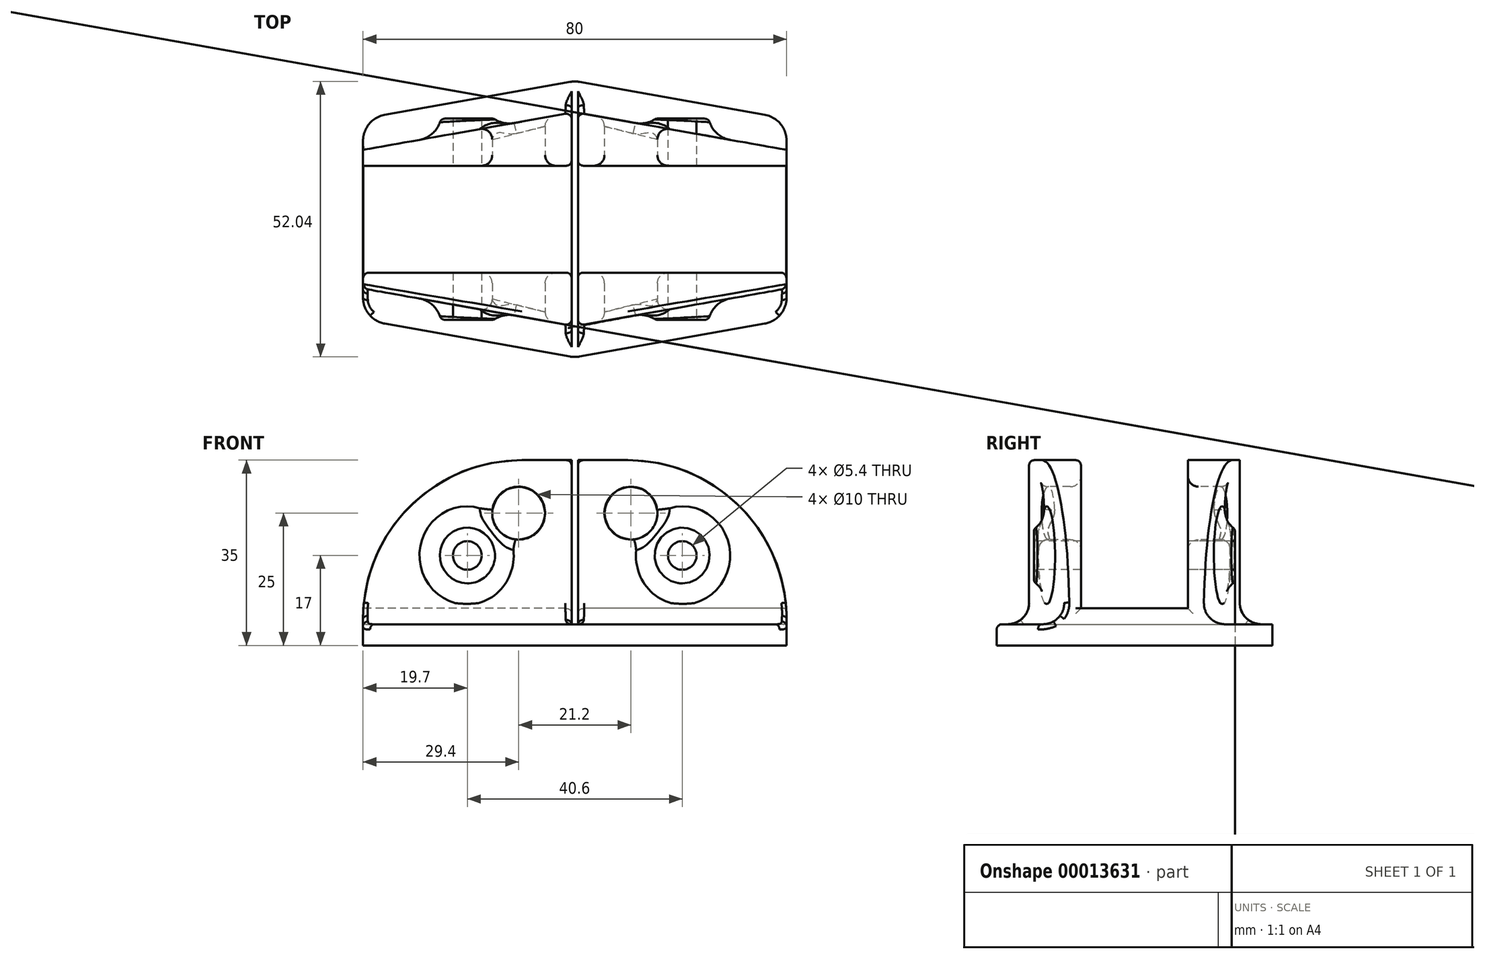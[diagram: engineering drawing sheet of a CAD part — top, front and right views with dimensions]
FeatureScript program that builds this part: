
annotation { "Feature Type Name" : "Feature", "Feature Type Description" : "" }
export const myFeature = defineFeature(function(context is Context, id is Id, definition is map)
    precondition{}
    {
        {
            var Q0;
            Q0=qCreatedBy(makeId("Top.planeOp"),FACE);
            var sketch = newSketch(context, id + "F0", { "sketchPlane" : qUnion([Q0])});
            skLineSegment(sketch, "E0.rect.bottom", {"start": v(40, 10.1) * mm, "end": v(-40, 10.1) * mm});
            skLineSegment(sketch, "E0.rect.top", {"start": v(40, -10.1) * mm, "end": v(-40, -10.1) * mm});
            skLineSegment(sketch, "E0.rect.left", {"start": v(40, 10.1) * mm, "end": v(40, -10.1) * mm});
            skLineSegment(sketch, "E0.rect.right", {"start": v(-40, 10.1) * mm, "end": v(-40, -10.1) * mm});
            skPoint(sketch, "E0.rect.middle", {"position": v(0, 0) * mm});
            skLineSegment(sketch, "E1", {"start": v(-40, 20.1) * mm, "end": v(40, 20.1) * mm, "construction": true});
            skLineSegment(sketch, "E2", {"start": v(40, -20.1) * mm, "end": v(-40, -20.1) * mm, "construction": true});
            skLineSegment(sketch, "E3", {"start": v(40, 10.1) * mm, "end": v(40, 20.1) * mm});
            skLineSegment(sketch, "E4", {"start": v(40, -10.1) * mm, "end": v(40, -20.1) * mm});
            skLineSegment(sketch, "E5.rect.bottom", {"start": v(0.6, 20.1) * mm, "end": v(-0.6, 20.1) * mm});
            skLineSegment(sketch, "E5.rect.top", {"start": v(0.6, -20.1) * mm, "end": v(-0.6, -20.1) * mm});
            skLineSegment(sketch, "E5.rect.left", {"start": v(0.6, 20.1) * mm, "end": v(0.6, 10.1) * mm});
            skLineSegment(sketch, "E5.rect.right", {"start": v(-0.6, 20.1) * mm, "end": v(-0.6, 10.1) * mm});
            skLineSegment(sketch, "E6", {"start": v(-40, -10.1) * mm, "end": v(-40, -20.1) * mm});
            skLineSegment(sketch, "E7", {"start": v(-40, 10.1) * mm, "end": v(-40, 20.1) * mm});
            skLineSegment(sketch, "E8.trimOffspring", {"start": v(0.6, -10.1) * mm, "end": v(0.6, -20.1) * mm});
            skLineSegment(sketch, "E9.trimOffspring", {"start": v(-0.6, -10.1) * mm, "end": v(-0.6, -20.1) * mm});
            skLineSegment(sketch, "E10", {"start": v(-40, 26.1) * mm, "end": v(40, 26.1) * mm, "construction": true});
            skLineSegment(sketch, "E11", {"start": v(40, -26.1) * mm, "end": v(-40, -26.1) * mm, "construction": true});
            skLineSegment(sketch, "E12", {"start": v(40, -20.1) * mm, "end": v(40, -26.1) * mm});
            skLineSegment(sketch, "E13", {"start": v(-40, -26.1) * mm, "end": v(-40, -20.1) * mm});
            skLineSegment(sketch, "E14", {"start": v(-40, 20.1) * mm, "end": v(-40, 26.1) * mm});
            skLineSegment(sketch, "E15", {"start": v(40, 26.1) * mm, "end": v(40, 20.1) * mm});
            skLineSegment(sketch, "E16", {"start": v(0.6, 10.1) * mm, "end": v(0.6, -10.1) * mm});
            skLineSegment(sketch, "E17", {"start": v(-0.6, -10.1) * mm, "end": v(-0.6, 10.1) * mm});
            skLineSegment(sketch, "E18", {"start": v(0.6, 20.1) * mm, "end": v(40, 13.1) * mm});
            skLineSegment(sketch, "E19", {"start": v(-0.6, 20.1) * mm, "end": v(-40, 13.1) * mm});
            skLineSegment(sketch, "E20", {"start": v(40, -13.1) * mm, "end": v(0.6, -20.1) * mm});
            skLineSegment(sketch, "E21", {"start": v(-0.6, -20.1) * mm, "end": v(-40, -13.1) * mm});
            skLineSegment(sketch, "E22", {"start": v(0, 26.1) * mm, "end": v(40, 19) * mm});
            skLineSegment(sketch, "E23", {"start": v(0, 26.1) * mm, "end": v(-40, 19) * mm});
            skLineSegment(sketch, "E24", {"start": v(0, -26.1) * mm, "end": v(40, -19) * mm});
            skLineSegment(sketch, "E25", {"start": v(0, -26.1) * mm, "end": v(-40, -19) * mm});
            skSolve(sketch);
        }
        {
            var Q0;
            Q0=makeQuery(id+"F0.imprint","IMPRINT",FACE,{"disambiguationData":[TD([[makeQuery(id+"F0.imprint","IMPRINT",EDGE,{"derivedFrom":sQuery(id+"F0.wireOp",EDGE,"E5.rect.bottom")}),-1.0]])]});
            var Q1;
            {var subQ4=sQuery(id+"F0.wireOp",EDGE,"E5.rect.right");Q1=makeQuery(id+"F0.imprint","IMPRINT",FACE,{"disambiguationData":[TD([[makeQuery(id+"F0.imprint","IMPRINT",EDGE,{"derivedFrom":subQ4}),-1.0]])]});}
            var Q2;
            Q2=makeQuery(id+"F0.imprint","IMPRINT",FACE,{"disambiguationData":[TD([[makeQuery(id+"F0.imprint","IMPRINT",EDGE,{"derivedFrom":sQuery(id+"F0.wireOp",EDGE,"E5.rect.bottom")}),1.0]])]});
            var Q3;
            {var subQ1=sQuery(id+"F0.wireOp",EDGE,"E5.rect.left");Q3=makeQuery(id+"F0.imprint","IMPRINT",FACE,{"disambiguationData":[TD([[makeQuery(id+"F0.imprint","IMPRINT",EDGE,{"derivedFrom":subQ1}),1.0]])]});}
            var Q4;
            {var subQ1=sQuery(id+"F0.wireOp",EDGE,"E0.rect.left");Q4=makeQuery(id+"F0.imprint","IMPRINT",FACE,{"disambiguationData":[TD([[makeQuery(id+"F0.imprint","IMPRINT",EDGE,{"derivedFrom":subQ1}),-1.0]])]});}
            var Q5;
            Q5=makeQuery(id+"F0.imprint","IMPRINT",FACE,{"disambiguationData":[TD([[makeQuery(id+"F0.imprint","IMPRINT",EDGE,{"derivedFrom":sQuery(id+"F0.wireOp",EDGE,"E5.rect.top")}),-1.0]])]});
            var Q6;
            {var subQ1=sQuery(id+"F0.wireOp",EDGE,"E9.trimOffspring");Q6=makeQuery(id+"F0.imprint","IMPRINT",FACE,{"disambiguationData":[TD([[makeQuery(id+"F0.imprint","IMPRINT",EDGE,{"derivedFrom":subQ1}),-1.0]])]});}
            var Q7;
            {var subQ1=sQuery(id+"F0.wireOp",EDGE,"E8.trimOffspring");Q7=makeQuery(id+"F0.imprint","IMPRINT",FACE,{"disambiguationData":[TD([[makeQuery(id+"F0.imprint","IMPRINT",EDGE,{"derivedFrom":subQ1}),1.0]])]});}
            var Q8;
            Q8=makeQuery(id+"F0.imprint","IMPRINT",FACE,{"disambiguationData":[TD([[makeQuery(id+"F0.imprint","IMPRINT",EDGE,{"derivedFrom":sQuery(id+"F0.wireOp",EDGE,"E5.rect.top")}),1.0]])]});
            var Q9;
            {var subQ1=sQuery(id+"F0.wireOp",EDGE,"E16");Q9=makeQuery(id+"F0.imprint","IMPRINT",FACE,{"disambiguationData":[TD([[makeQuery(id+"F0.imprint","IMPRINT",EDGE,{"derivedFrom":subQ1}),-1.0]])]});}
            var Q10;
            {var subQ1=sQuery(id+"F0.wireOp",EDGE,"E0.rect.right");Q10=makeQuery(id+"F0.imprint","IMPRINT",FACE,{"disambiguationData":[TD([[makeQuery(id+"F0.imprint","IMPRINT",EDGE,{"derivedFrom":subQ1}),1.0]])]});}
            extrude(context, id + "F1", {"entities" : qUnion([Q0, Q1, Q2, Q3, Q4, Q5, Q6, Q7, Q8, Q9, Q10]), "depth" : 4 * mm});
        }
        {
            var Q0;
            {var subQ1=sQuery(id+"F0.wireOp",EDGE,"E9.trimOffspring");Q0=makeQuery(id+"F0.imprint","IMPRINT",FACE,{"disambiguationData":[TD([[makeQuery(id+"F0.imprint","IMPRINT",EDGE,{"derivedFrom":subQ1}),-1.0]])]});}
            var Q1;
            {var subQ1=sQuery(id+"F0.wireOp",EDGE,"E8.trimOffspring");Q1=makeQuery(id+"F0.imprint","IMPRINT",FACE,{"disambiguationData":[TD([[makeQuery(id+"F0.imprint","IMPRINT",EDGE,{"derivedFrom":subQ1}),1.0]])]});}
            var Q2;
            {var subQ1=sQuery(id+"F0.wireOp",EDGE,"E5.rect.left");Q2=makeQuery(id+"F0.imprint","IMPRINT",FACE,{"disambiguationData":[TD([[makeQuery(id+"F0.imprint","IMPRINT",EDGE,{"derivedFrom":subQ1}),1.0]])]});}
            var Q3;
            {var subQ4=sQuery(id+"F0.wireOp",EDGE,"E5.rect.right");Q3=makeQuery(id+"F0.imprint","IMPRINT",FACE,{"disambiguationData":[TD([[makeQuery(id+"F0.imprint","IMPRINT",EDGE,{"derivedFrom":subQ4}),-1.0]])]});}
            extrude(context, id + "F2", {"entities" : qUnion([Q0, Q1, Q2, Q3]), "operationType" : NewBodyOperationType.ADD, "depth" : 35 * mm});
        }
        {
            var Q0;
            {var subQ1=sQuery(id+"F0.wireOp",EDGE,"E0.rect.right");Q0=makeQuery(id+"F0.imprint","IMPRINT",FACE,{"disambiguationData":[TD([[makeQuery(id+"F0.imprint","IMPRINT",EDGE,{"derivedFrom":subQ1}),1.0]])]});}
            var Q1;
            {var subQ1=sQuery(id+"F0.wireOp",EDGE,"E0.rect.left");Q1=makeQuery(id+"F0.imprint","IMPRINT",FACE,{"disambiguationData":[TD([[makeQuery(id+"F0.imprint","IMPRINT",EDGE,{"derivedFrom":subQ1}),-1.0]])]});}
            extrude(context, id + "F3", {"entities" : qUnion([Q0, Q1]), "operationType" : NewBodyOperationType.ADD, "depth" : 7 * mm});
        }
        {
            var Q0;
            Q0=qCreatedBy(makeId("Front.planeOp"),FACE);
            var sketch = newSketch(context, id + "F4", { "sketchPlane" : qUnion([Q0])});
            skLineSegment(sketch, "E26.0", {"start": v(-0.6, 7) * mm, "end": v(-40, 7) * mm});
            skLineSegment(sketch, "E27.0", {"start": v(40, 7) * mm, "end": v(0.6, 7) * mm});
            skLineSegment(sketch, "E28", {"start": v(-20.3, 7) * mm, "end": v(-20.3, 17) * mm, "construction": true});
            skLineSegment(sketch, "E29", {"start": v(20.3, 7) * mm, "end": v(20.3, 17) * mm, "construction": true});
            skCircle(sketch, "E30", {"center": v(-20.3, 17) * mm, "radius": 2.7 * mm});
            skCircle(sketch, "E31", {"center": v(20.3, 17) * mm, "radius": 2.7 * mm});
            skCircle(sketch, "E32", {"center": v(-20.3, 17) * mm, "radius": 5 * mm});
            skCircle(sketch, "E33", {"center": v(20.3, 17) * mm, "radius": 5 * mm});
            skCircle(sketch, "E34", {"center": v(-10.6, 25) * mm, "radius": 5 * mm});
            skCircle(sketch, "E35", {"center": v(10.6, 25) * mm, "radius": 5 * mm});
            skLineSegment(sketch, "E36.0", {"start": v(-0.6, 35) * mm, "end": v(-0.6, 7) * mm});
            skLineSegment(sketch, "E37.0", {"start": v(0.6, 35) * mm, "end": v(0.6, 7) * mm});
            skLineSegment(sketch, "E38", {"start": v(-10.6, 25) * mm, "end": v(-0.6, 25) * mm, "construction": true});
            skLineSegment(sketch, "E39", {"start": v(10.6, 25) * mm, "end": v(0.6, 25) * mm, "construction": true});
            skSolve(sketch);
        }
        {
            var Q0;
            Q0=makeQuery(id+"F4.imprint","IMPRINT",FACE,{"disambiguationData":[TD([[makeQuery(id+"F4.imprint","IMPRINT",EDGE,{"derivedFrom":sQuery(id+"F4.wireOp",EDGE,"E30")}),1.0]])]});
            var Q1;
            Q1=makeQuery(id+"F4.imprint","IMPRINT",FACE,{"disambiguationData":[TD([[makeQuery(id+"F4.imprint","IMPRINT",EDGE,{"derivedFrom":sQuery(id+"F4.wireOp",EDGE,"E31")}),1.0]])]});
            extrude(context, id + "F5", {"entities" : qUnion([Q0, Q1]), "operationType" : NewBodyOperationType.REMOVE, "oppositeDirection" : true, "depth" : 50 * mm, "symmetric" : true});
        }
        {
            var Q0;
            Q0=makeQuery(id+"F4.imprint","IMPRINT",FACE,{"disambiguationData":[TD([[makeQuery(id+"F4.imprint","IMPRINT",EDGE,{"derivedFrom":sQuery(id+"F4.wireOp",EDGE,"E30")}),-1.0]])]});
            var Q1;
            Q1=makeQuery(id+"F4.imprint","IMPRINT",FACE,{"disambiguationData":[TD([[makeQuery(id+"F4.imprint","IMPRINT",EDGE,{"derivedFrom":sQuery(id+"F4.wireOp",EDGE,"E31")}),-1.0]])]});
            extrude(context, id + "F6", {"entities" : qUnion([Q0, Q1]), "operationType" : NewBodyOperationType.ADD, "depth" : 38 * mm, "symmetric" : true});
        }
        {
            var Q0;
            Q0=makeQuery(id+"F4.imprint","IMPRINT",FACE,{"disambiguationData":[TD([[makeQuery(id+"F4.imprint","IMPRINT",EDGE,{"derivedFrom":sQuery(id+"F4.wireOp",EDGE,"E30")}),-1.0]])]});
            var Q1;
            Q1=makeQuery(id+"F4.imprint","IMPRINT",FACE,{"disambiguationData":[TD([[makeQuery(id+"F4.imprint","IMPRINT",EDGE,{"derivedFrom":sQuery(id+"F4.wireOp",EDGE,"E31")}),-1.0]])]});
            extrude(context, id + "F7", {"entities" : qUnion([Q0, Q1]), "operationType" : NewBodyOperationType.REMOVE, "oppositeDirection" : true, "depth" : 20.2 * mm, "symmetric" : true});
        }
        {
            var Q0;
            Q0=makeQuery(id+"F4.imprint","IMPRINT",FACE,{"disambiguationData":[TD([[makeQuery(id+"F4.imprint","IMPRINT",EDGE,{"derivedFrom":sQuery(id+"F4.wireOp",EDGE,"E34")}),1.0]])]});
            var Q1;
            Q1=makeQuery(id+"F4.imprint","IMPRINT",FACE,{"disambiguationData":[TD([[makeQuery(id+"F4.imprint","IMPRINT",EDGE,{"derivedFrom":sQuery(id+"F4.wireOp",EDGE,"E35")}),1.0]])]});
            extrude(context, id + "F8", {"entities" : qUnion([Q0, Q1]), "operationType" : NewBodyOperationType.REMOVE, "oppositeDirection" : true, "depth" : 50 * mm, "symmetric" : true});
        }
        {
            var Q0;
            Q0=makeQuery(id+"F2.opExtrude","CAP_EDGE",EDGE,{"disambiguationData":[OSD([sQuery(id+"F0.wireOp",EDGE,"E4")])],"isStart":false});
            var Q1;
            Q1=makeQuery(id+"F2.opExtrude","CAP_EDGE",EDGE,{"disambiguationData":[OSD([sQuery(id+"F0.wireOp",EDGE,"E6")])],"isStart":false});
            var Q2;
            Q2=makeQuery(id+"F2.opExtrude","CAP_EDGE",EDGE,{"disambiguationData":[OSD([sQuery(id+"F0.wireOp",EDGE,"E7")])],"isStart":false});
            var Q3;
            Q3=makeQuery(id+"F2.opExtrude","CAP_EDGE",EDGE,{"disambiguationData":[OSD([sQuery(id+"F0.wireOp",EDGE,"E3")])],"isStart":false});
            fillet(context, id + "F9", {"entities" : qUnion([Q0, Q1, Q2, Q3]), "radius" : 30 * mm, "tangentPropagation" : true, "allowEdgeOverflow" : false});
        }
        {
            var Q0;
            Q0=makeQuery(id+"F1.opExtrude","SWEPT_EDGE",EDGE,{"disambiguationData":[OSD([sQuery(id+"F0.wireOp",EDGE,"E7"),sQuery(id+"F0.wireOp",EDGE,"E23")])]});
            var Q1;
            Q1=makeQuery(id+"F1.opExtrude","SWEPT_EDGE",EDGE,{"disambiguationData":[OSD([sQuery(id+"F0.wireOp",EDGE,"E6"),sQuery(id+"F0.wireOp",EDGE,"E25")])]});
            var Q2;
            Q2=makeQuery(id+"F1.opExtrude","SWEPT_EDGE",EDGE,{"disambiguationData":[OSD([sQuery(id+"F0.wireOp",EDGE,"E22"),sQuery(id+"F0.wireOp",EDGE,"E23")])]});
            var Q3;
            Q3=makeQuery(id+"F1.opExtrude","SWEPT_EDGE",EDGE,{"disambiguationData":[OSD([sQuery(id+"F0.wireOp",EDGE,"E3"),sQuery(id+"F0.wireOp",EDGE,"E22")])]});
            var Q4;
            Q4=makeQuery(id+"F1.opExtrude","SWEPT_EDGE",EDGE,{"disambiguationData":[OSD([sQuery(id+"F0.wireOp",EDGE,"E4"),sQuery(id+"F0.wireOp",EDGE,"E24")])]});
            var Q5;
            Q5=makeQuery(id+"F1.opExtrude","SWEPT_EDGE",EDGE,{"disambiguationData":[OSD([sQuery(id+"F0.wireOp",EDGE,"E24"),sQuery(id+"F0.wireOp",EDGE,"E25")])]});
            fillet(context, id + "F10", {"entities" : qUnion([Q0, Q1, Q2, Q3, Q4, Q5]), "radius" : 5 * mm, "tangentPropagation" : true, "allowEdgeOverflow" : false});
        }
        {
            var Q0;
            Q0=makeQuery(id+"F2.boolean.opBoolean","INTERSECT",EDGE,{"derivedFrom":[makeQuery(id+"F1.opExtrude","CAP_FACE",FACE,{"disambiguationData":[OSD([sQuery(id+"F0.wireOp",EDGE,"E0.rect.left"),sQuery(id+"F0.wireOp",EDGE,"E0.rect.right"),sQuery(id+"F0.wireOp",EDGE,"E3"),sQuery(id+"F0.wireOp",EDGE,"E4"),sQuery(id+"F0.wireOp",EDGE,"E6"),sQuery(id+"F0.wireOp",EDGE,"E7"),sQuery(id+"F0.wireOp",EDGE,"E22"),sQuery(id+"F0.wireOp",EDGE,"E23"),sQuery(id+"F0.wireOp",EDGE,"E24"),sQuery(id+"F0.wireOp",EDGE,"E25")])],"isStart":false}),makeQuery(id+"F2.opExtrude","SWEPT_FACE",FACE,{"disambiguationData":[OSD([sQuery(id+"F0.wireOp",EDGE,"E21")])]})]});
            var Q1;
            Q1=makeQuery(id+"F2.boolean.opBoolean","INTERSECT",EDGE,{"derivedFrom":[makeQuery(id+"F1.opExtrude","CAP_FACE",FACE,{"disambiguationData":[OSD([sQuery(id+"F0.wireOp",EDGE,"E0.rect.left"),sQuery(id+"F0.wireOp",EDGE,"E0.rect.right"),sQuery(id+"F0.wireOp",EDGE,"E3"),sQuery(id+"F0.wireOp",EDGE,"E4"),sQuery(id+"F0.wireOp",EDGE,"E6"),sQuery(id+"F0.wireOp",EDGE,"E7"),sQuery(id+"F0.wireOp",EDGE,"E22"),sQuery(id+"F0.wireOp",EDGE,"E23"),sQuery(id+"F0.wireOp",EDGE,"E24"),sQuery(id+"F0.wireOp",EDGE,"E25")])],"isStart":false}),makeQuery(id+"F2.opExtrude","SWEPT_FACE",FACE,{"disambiguationData":[OSD([sQuery(id+"F0.wireOp",EDGE,"E20")])]})]});
            var Q2;
            Q2=makeQuery(id+"F2.boolean.opBoolean","INTERSECT",EDGE,{"derivedFrom":[makeQuery(id+"F1.opExtrude","CAP_FACE",FACE,{"disambiguationData":[OSD([sQuery(id+"F0.wireOp",EDGE,"E0.rect.left"),sQuery(id+"F0.wireOp",EDGE,"E0.rect.right"),sQuery(id+"F0.wireOp",EDGE,"E3"),sQuery(id+"F0.wireOp",EDGE,"E4"),sQuery(id+"F0.wireOp",EDGE,"E6"),sQuery(id+"F0.wireOp",EDGE,"E7"),sQuery(id+"F0.wireOp",EDGE,"E22"),sQuery(id+"F0.wireOp",EDGE,"E23"),sQuery(id+"F0.wireOp",EDGE,"E24"),sQuery(id+"F0.wireOp",EDGE,"E25")])],"isStart":false}),makeQuery(id+"F2.opExtrude","SWEPT_FACE",FACE,{"disambiguationData":[OSD([sQuery(id+"F0.wireOp",EDGE,"E19")])]})]});
            var Q3;
            Q3=makeQuery(id+"F2.boolean.opBoolean","INTERSECT",EDGE,{"derivedFrom":[makeQuery(id+"F1.opExtrude","CAP_FACE",FACE,{"disambiguationData":[OSD([sQuery(id+"F0.wireOp",EDGE,"E0.rect.left"),sQuery(id+"F0.wireOp",EDGE,"E0.rect.right"),sQuery(id+"F0.wireOp",EDGE,"E3"),sQuery(id+"F0.wireOp",EDGE,"E4"),sQuery(id+"F0.wireOp",EDGE,"E6"),sQuery(id+"F0.wireOp",EDGE,"E7"),sQuery(id+"F0.wireOp",EDGE,"E22"),sQuery(id+"F0.wireOp",EDGE,"E23"),sQuery(id+"F0.wireOp",EDGE,"E24"),sQuery(id+"F0.wireOp",EDGE,"E25")])],"isStart":false}),makeQuery(id+"F2.opExtrude","SWEPT_FACE",FACE,{"disambiguationData":[OSD([sQuery(id+"F0.wireOp",EDGE,"E18")])]})]});
            fillet(context, id + "F11", {"entities" : qUnion([Q0, Q1, Q2, Q3]), "radius" : 4 * mm, "tangentPropagation" : true, "allowEdgeOverflow" : false});
        }
        {
            var Q0;
            Q0=makeQuery(id+"F11.opFillet","BLEND_EDGE",EDGE,{"blendedFrom":[makeQuery(id+"F2.boolean.opBoolean","INTERSECT",EDGE,{"derivedFrom":[makeQuery(id+"F1.opExtrude","CAP_FACE",FACE,{"disambiguationData":[OSD([sQuery(id+"F0.wireOp",EDGE,"E0.rect.left"),sQuery(id+"F0.wireOp",EDGE,"E0.rect.right"),sQuery(id+"F0.wireOp",EDGE,"E3"),sQuery(id+"F0.wireOp",EDGE,"E4"),sQuery(id+"F0.wireOp",EDGE,"E6"),sQuery(id+"F0.wireOp",EDGE,"E7"),sQuery(id+"F0.wireOp",EDGE,"E22"),sQuery(id+"F0.wireOp",EDGE,"E23"),sQuery(id+"F0.wireOp",EDGE,"E24"),sQuery(id+"F0.wireOp",EDGE,"E25")])],"isStart":false}),makeQuery(id+"F2.opExtrude","SWEPT_FACE",FACE,{"disambiguationData":[OSD([sQuery(id+"F0.wireOp",EDGE,"E18")])]})]}),makeQuery(id+"F3.boolean.opBoolean","MERGE",FACE,{"derivedFrom":[makeQuery(id+"F2.opExtrude","SWEPT_FACE",FACE,{"disambiguationData":[OSD([sQuery(id+"F0.wireOp",EDGE,"E5.rect.left")])]}),makeQuery(id+"F2.opExtrude","SWEPT_FACE",FACE,{"disambiguationData":[OSD([sQuery(id+"F0.wireOp",EDGE,"E8.trimOffspring")])]}),makeQuery(id+"F3.opExtrude","SWEPT_FACE",FACE,{"disambiguationData":[OSD([sQuery(id+"F0.wireOp",EDGE,"E16")])]})]})],"blendedInto":[makeQuery(id+"F3.boolean.opBoolean","MERGE",FACE,{"derivedFrom":[makeQuery(id+"F2.opExtrude","SWEPT_FACE",FACE,{"disambiguationData":[OSD([sQuery(id+"F0.wireOp",EDGE,"E5.rect.left")])]}),makeQuery(id+"F2.opExtrude","SWEPT_FACE",FACE,{"disambiguationData":[OSD([sQuery(id+"F0.wireOp",EDGE,"E8.trimOffspring")])]}),makeQuery(id+"F3.opExtrude","SWEPT_FACE",FACE,{"disambiguationData":[OSD([sQuery(id+"F0.wireOp",EDGE,"E16")])]})]})]});
            var Q1;
            Q1=makeQuery(id+"F11.opFillet","BLEND_EDGE",EDGE,{"blendedFrom":[makeQuery(id+"F2.boolean.opBoolean","INTERSECT",EDGE,{"derivedFrom":[makeQuery(id+"F1.opExtrude","CAP_FACE",FACE,{"disambiguationData":[OSD([sQuery(id+"F0.wireOp",EDGE,"E0.rect.left"),sQuery(id+"F0.wireOp",EDGE,"E0.rect.right"),sQuery(id+"F0.wireOp",EDGE,"E3"),sQuery(id+"F0.wireOp",EDGE,"E4"),sQuery(id+"F0.wireOp",EDGE,"E6"),sQuery(id+"F0.wireOp",EDGE,"E7"),sQuery(id+"F0.wireOp",EDGE,"E22"),sQuery(id+"F0.wireOp",EDGE,"E23"),sQuery(id+"F0.wireOp",EDGE,"E24"),sQuery(id+"F0.wireOp",EDGE,"E25")])],"isStart":false}),makeQuery(id+"F2.opExtrude","SWEPT_FACE",FACE,{"disambiguationData":[OSD([sQuery(id+"F0.wireOp",EDGE,"E19")])]})]}),makeQuery(id+"F3.boolean.opBoolean","MERGE",FACE,{"derivedFrom":[makeQuery(id+"F2.opExtrude","SWEPT_FACE",FACE,{"disambiguationData":[OSD([sQuery(id+"F0.wireOp",EDGE,"E5.rect.right")])]}),makeQuery(id+"F2.opExtrude","SWEPT_FACE",FACE,{"disambiguationData":[OSD([sQuery(id+"F0.wireOp",EDGE,"E9.trimOffspring")])]}),makeQuery(id+"F3.opExtrude","SWEPT_FACE",FACE,{"disambiguationData":[OSD([sQuery(id+"F0.wireOp",EDGE,"E17")])]})]})],"blendedInto":[makeQuery(id+"F3.boolean.opBoolean","MERGE",FACE,{"derivedFrom":[makeQuery(id+"F2.opExtrude","SWEPT_FACE",FACE,{"disambiguationData":[OSD([sQuery(id+"F0.wireOp",EDGE,"E5.rect.right")])]}),makeQuery(id+"F2.opExtrude","SWEPT_FACE",FACE,{"disambiguationData":[OSD([sQuery(id+"F0.wireOp",EDGE,"E9.trimOffspring")])]}),makeQuery(id+"F3.opExtrude","SWEPT_FACE",FACE,{"disambiguationData":[OSD([sQuery(id+"F0.wireOp",EDGE,"E17")])]})]})]});
            var Q2;
            Q2=makeQuery(id+"F2.opExtrude","SWEPT_EDGE",EDGE,{"disambiguationData":[OSD([sQuery(id+"F0.wireOp",EDGE,"E0.rect.bottom"),sQuery(id+"F0.wireOp",EDGE,"E5.rect.right"),sQuery(id+"F0.wireOp",EDGE,"E17")])]});
            var Q3;
            Q3=makeQuery(id+"F2.opExtrude","SWEPT_EDGE",EDGE,{"disambiguationData":[OSD([sQuery(id+"F0.wireOp",EDGE,"E0.rect.bottom"),sQuery(id+"F0.wireOp",EDGE,"E5.rect.left"),sQuery(id+"F0.wireOp",EDGE,"E16")])]});
            var Q4;
            Q4=makeQuery(id+"F2.opExtrude","SWEPT_EDGE",EDGE,{"disambiguationData":[OSD([sQuery(id+"F0.wireOp",EDGE,"E5.rect.top"),sQuery(id+"F0.wireOp",EDGE,"E8.trimOffspring"),sQuery(id+"F0.wireOp",EDGE,"E20")])]});
            var Q5;
            Q5=makeQuery(id+"F2.opExtrude","SWEPT_EDGE",EDGE,{"disambiguationData":[OSD([sQuery(id+"F0.wireOp",EDGE,"E5.rect.top"),sQuery(id+"F0.wireOp",EDGE,"E9.trimOffspring"),sQuery(id+"F0.wireOp",EDGE,"E21")])]});
            var Q6;
            Q6=makeQuery(id+"F2.opExtrude","SWEPT_EDGE",EDGE,{"disambiguationData":[OSD([sQuery(id+"F0.wireOp",EDGE,"E0.rect.top"),sQuery(id+"F0.wireOp",EDGE,"E9.trimOffspring"),sQuery(id+"F0.wireOp",EDGE,"E17")])]});
            var Q7;
            Q7=makeQuery(id+"F2.opExtrude","SWEPT_EDGE",EDGE,{"disambiguationData":[OSD([sQuery(id+"F0.wireOp",EDGE,"E0.rect.top"),sQuery(id+"F0.wireOp",EDGE,"E8.trimOffspring"),sQuery(id+"F0.wireOp",EDGE,"E16")])]});
            var Q8;
            Q8=makeQuery(id+"F3.opExtrude","CAP_EDGE",EDGE,{"disambiguationData":[OSD([sQuery(id+"F0.wireOp",EDGE,"E17")])],"isStart":false});
            var Q9;
            Q9=makeQuery(id+"F3.opExtrude","CAP_EDGE",EDGE,{"disambiguationData":[OSD([sQuery(id+"F0.wireOp",EDGE,"E16")])],"isStart":false});
            var Q10;
            {var subQ0=sQuery(id+"F0.wireOp",EDGE,"E0.rect.top");Q10=makeQuery(id+"F3.opExtrude","CAP_EDGE",EDGE,{"disambiguationData":[OSD([subQ0]),TDD([makeQuery(id+"F0.imprint","IMPRINT",EDGE,{"disambiguationData":[TD([[makeQuery(id+"F0.imprint","INTERSECT",VERTEX,{"derivedFrom":[subQ0,sQuery(id+"F0.wireOp",EDGE,"E0.rect.left"),sQuery(id+"F0.wireOp",EDGE,"E4")]}),-1.0]])],"derivedFrom":subQ0})])],"isStart":false});}
            var Q11;
            {var subQ0=sQuery(id+"F0.wireOp",EDGE,"E0.rect.bottom");Q11=makeQuery(id+"F3.opExtrude","CAP_EDGE",EDGE,{"disambiguationData":[OSD([subQ0]),TDD([makeQuery(id+"F0.imprint","IMPRINT",EDGE,{"disambiguationData":[TD([[makeQuery(id+"F0.imprint","INTERSECT",VERTEX,{"derivedFrom":[subQ0,sQuery(id+"F0.wireOp",EDGE,"E0.rect.left"),sQuery(id+"F0.wireOp",EDGE,"E3")]}),-1.0]])],"derivedFrom":subQ0})])],"isStart":false});}
            var Q12;
            {var subQ0=sQuery(id+"F0.wireOp",EDGE,"E0.rect.bottom");Q12=makeQuery(id+"F3.opExtrude","CAP_EDGE",EDGE,{"disambiguationData":[OSD([subQ0]),TDD([makeQuery(id+"F0.imprint","IMPRINT",EDGE,{"disambiguationData":[TD([[makeQuery(id+"F0.imprint","INTERSECT",VERTEX,{"derivedFrom":[subQ0,sQuery(id+"F0.wireOp",EDGE,"E0.rect.right"),sQuery(id+"F0.wireOp",EDGE,"E7")]}),1.0]])],"derivedFrom":subQ0})])],"isStart":false});}
            var Q13;
            {var subQ0=sQuery(id+"F0.wireOp",EDGE,"E0.rect.top");Q13=makeQuery(id+"F3.opExtrude","CAP_EDGE",EDGE,{"disambiguationData":[OSD([subQ0]),TDD([makeQuery(id+"F0.imprint","IMPRINT",EDGE,{"disambiguationData":[TD([[makeQuery(id+"F0.imprint","INTERSECT",VERTEX,{"derivedFrom":[subQ0,sQuery(id+"F0.wireOp",EDGE,"E0.rect.right"),sQuery(id+"F0.wireOp",EDGE,"E6")]}),1.0]])],"derivedFrom":subQ0})])],"isStart":false});}
            var Q14;
            Q14=makeQuery(id+"F3.opExtrude","CAP_EDGE",EDGE,{"disambiguationData":[OSD([sQuery(id+"F0.wireOp",EDGE,"E0.rect.right")])],"isStart":false});
            var Q15;
            Q15=makeQuery(id+"F3.opExtrude","CAP_EDGE",EDGE,{"disambiguationData":[OSD([sQuery(id+"F0.wireOp",EDGE,"E0.rect.left")])],"isStart":false});
            fillet(context, id + "F12", {"entities" : qUnion([Q0, Q1, Q2, Q3, Q4, Q5, Q6, Q7, Q8, Q9, Q10, Q11, Q12, Q13, Q14, Q15]), "radius" : 1 * mm, "tangentPropagation" : true, "allowEdgeOverflow" : false});
        }
        {
            var Q0;
            Q0=makeQuery(id+"F9.opFillet","BLEND_EDGE",EDGE,{"blendedFrom":[makeQuery(id+"F2.opExtrude","CAP_EDGE",EDGE,{"disambiguationData":[OSD([sQuery(id+"F0.wireOp",EDGE,"E4")])],"isStart":false}),makeQuery(id+"F2.opExtrude","SWEPT_FACE",FACE,{"disambiguationData":[OSD([sQuery(id+"F0.wireOp",EDGE,"E20")])]})],"blendedInto":[makeQuery(id+"F2.opExtrude","SWEPT_FACE",FACE,{"disambiguationData":[OSD([sQuery(id+"F0.wireOp",EDGE,"E20")])]})]});
            var Q1;
            {var subQ0=sQuery(id+"F0.wireOp",EDGE,"E3");var subQ1=sQuery(id+"F0.wireOp",EDGE,"E18");Q1=makeQuery(id+"F9.opFillet","BLEND_EDGE",EDGE,{"blendedFrom":[makeQuery(id+"F2.opExtrude","CAP_EDGE",EDGE,{"disambiguationData":[OSD([subQ0])],"isStart":false}),makeQuery(id+"F6.boolean.opBoolean","SPLIT",FACE,{"disambiguationData":[TD([makeQuery(id+"F2.opExtrude","SWEPT_FACE",FACE,{"disambiguationData":[OSD([subQ0])]})])],"derivedFrom":makeQuery(id+"F2.opExtrude","SWEPT_FACE",FACE,{"disambiguationData":[OSD([subQ1])]})})],"blendedInto":[makeQuery(id+"F6.boolean.opBoolean","SPLIT",FACE,{"disambiguationData":[TD([makeQuery(id+"F2.opExtrude","SWEPT_FACE",FACE,{"disambiguationData":[OSD([subQ0])]})])],"derivedFrom":makeQuery(id+"F2.opExtrude","SWEPT_FACE",FACE,{"disambiguationData":[OSD([subQ1])]})})]});}
            var Q2;
            Q2=makeQuery(id+"F9.opFillet","BLEND_EDGE",EDGE,{"blendedFrom":[makeQuery(id+"F2.opExtrude","CAP_EDGE",EDGE,{"disambiguationData":[OSD([sQuery(id+"F0.wireOp",EDGE,"E7")])],"isStart":false}),makeQuery(id+"F2.opExtrude","SWEPT_FACE",FACE,{"disambiguationData":[OSD([sQuery(id+"F0.wireOp",EDGE,"E19")])]})],"blendedInto":[makeQuery(id+"F2.opExtrude","SWEPT_FACE",FACE,{"disambiguationData":[OSD([sQuery(id+"F0.wireOp",EDGE,"E19")])]})]});
            var Q3;
            {var subQ0=sQuery(id+"F0.wireOp",EDGE,"E6");var subQ1=sQuery(id+"F0.wireOp",EDGE,"E21");Q3=makeQuery(id+"F9.opFillet","BLEND_EDGE",EDGE,{"blendedFrom":[makeQuery(id+"F2.opExtrude","CAP_EDGE",EDGE,{"disambiguationData":[OSD([subQ0])],"isStart":false}),makeQuery(id+"F6.boolean.opBoolean","SPLIT",FACE,{"disambiguationData":[TD([makeQuery(id+"F2.opExtrude","SWEPT_FACE",FACE,{"disambiguationData":[OSD([sQuery(id+"F0.wireOp",EDGE,"E5.rect.right")])]})])],"derivedFrom":makeQuery(id+"F2.opExtrude","SWEPT_FACE",FACE,{"disambiguationData":[OSD([subQ1])]})})],"blendedInto":[makeQuery(id+"F6.boolean.opBoolean","SPLIT",FACE,{"disambiguationData":[TD([makeQuery(id+"F2.opExtrude","SWEPT_FACE",FACE,{"disambiguationData":[OSD([sQuery(id+"F0.wireOp",EDGE,"E5.rect.right")])]})])],"derivedFrom":makeQuery(id+"F2.opExtrude","SWEPT_FACE",FACE,{"disambiguationData":[OSD([subQ1])]})})]});}
            fillet(context, id + "F13", {"entities" : qUnion([Q0, Q1, Q2, Q3]), "radius" : 1 * mm, "tangentPropagation" : true, "allowEdgeOverflow" : false});
        }
        {
            var Q0;
            Q0=makeQuery(id+"F6.boolean.opBoolean","INTERSECT",EDGE,{"derivedFrom":[makeQuery(id+"F2.opExtrude","SWEPT_FACE",FACE,{"disambiguationData":[OSD([sQuery(id+"F0.wireOp",EDGE,"E18")])]}),makeQuery(id+"F6.opExtrude","SWEPT_FACE",FACE,{"disambiguationData":[OSD([sQuery(id+"F4.wireOp",EDGE,"E33")])]})]});
            var Q1;
            Q1=makeQuery(id+"F6.boolean.opBoolean","INTERSECT",EDGE,{"derivedFrom":[makeQuery(id+"F2.opExtrude","SWEPT_FACE",FACE,{"disambiguationData":[OSD([sQuery(id+"F0.wireOp",EDGE,"E19")])]}),makeQuery(id+"F6.opExtrude","SWEPT_FACE",FACE,{"disambiguationData":[OSD([sQuery(id+"F4.wireOp",EDGE,"E32")])]})]});
            var Q2;
            Q2=makeQuery(id+"F6.boolean.opBoolean","INTERSECT",EDGE,{"derivedFrom":[makeQuery(id+"F2.opExtrude","SWEPT_FACE",FACE,{"disambiguationData":[OSD([sQuery(id+"F0.wireOp",EDGE,"E20")])]}),makeQuery(id+"F6.opExtrude","SWEPT_FACE",FACE,{"disambiguationData":[OSD([sQuery(id+"F4.wireOp",EDGE,"E33")])]})]});
            var Q3;
            Q3=makeQuery(id+"F6.boolean.opBoolean","INTERSECT",EDGE,{"derivedFrom":[makeQuery(id+"F2.opExtrude","SWEPT_FACE",FACE,{"disambiguationData":[OSD([sQuery(id+"F0.wireOp",EDGE,"E21")])]}),makeQuery(id+"F6.opExtrude","SWEPT_FACE",FACE,{"disambiguationData":[OSD([sQuery(id+"F4.wireOp",EDGE,"E32")])]})]});
            fillet(context, id + "F14", {"entities" : qUnion([Q0, Q1, Q2, Q3]), "radius" : 5 * mm, "tangentPropagation" : true, "allowEdgeOverflow" : false});
        }
        {
            var Q0;
            {var subQ0=sQuery(id+"F4.wireOp",EDGE,"E33");Q0=makeQuery(id+"F14.opFillet","BLEND_EDGE",EDGE,{"blendedFrom":[makeQuery(id+"F6.boolean.opBoolean","INTERSECT",EDGE,{"derivedFrom":[makeQuery(id+"F2.opExtrude","SWEPT_FACE",FACE,{"disambiguationData":[OSD([sQuery(id+"F0.wireOp",EDGE,"E20")])]}),makeQuery(id+"F6.opExtrude","SWEPT_FACE",FACE,{"disambiguationData":[OSD([subQ0])]})]}),makeQuery(id+"F6.opExtrude","CAP_FACE",FACE,{"disambiguationData":[OSD([sQuery(id+"F4.wireOp",EDGE,"E31"),subQ0])],"isStart":false})],"blendedInto":[makeQuery(id+"F6.opExtrude","CAP_FACE",FACE,{"disambiguationData":[OSD([sQuery(id+"F4.wireOp",EDGE,"E31"),subQ0])],"isStart":false})]});}
            var Q1;
            {var subQ0=sQuery(id+"F4.wireOp",EDGE,"E32");Q1=makeQuery(id+"F14.opFillet","BLEND_EDGE",EDGE,{"blendedFrom":[makeQuery(id+"F6.boolean.opBoolean","INTERSECT",EDGE,{"derivedFrom":[makeQuery(id+"F2.opExtrude","SWEPT_FACE",FACE,{"disambiguationData":[OSD([sQuery(id+"F0.wireOp",EDGE,"E21")])]}),makeQuery(id+"F6.opExtrude","SWEPT_FACE",FACE,{"disambiguationData":[OSD([subQ0])]})]}),makeQuery(id+"F6.opExtrude","CAP_FACE",FACE,{"disambiguationData":[OSD([sQuery(id+"F4.wireOp",EDGE,"E30"),subQ0])],"isStart":false})],"blendedInto":[makeQuery(id+"F6.opExtrude","CAP_FACE",FACE,{"disambiguationData":[OSD([sQuery(id+"F4.wireOp",EDGE,"E30"),subQ0])],"isStart":false})]});}
            var Q2;
            {var subQ0=sQuery(id+"F4.wireOp",EDGE,"E33");Q2=makeQuery(id+"F14.opFillet","BLEND_EDGE",EDGE,{"blendedFrom":[makeQuery(id+"F6.boolean.opBoolean","INTERSECT",EDGE,{"derivedFrom":[makeQuery(id+"F2.opExtrude","SWEPT_FACE",FACE,{"disambiguationData":[OSD([sQuery(id+"F0.wireOp",EDGE,"E18")])]}),makeQuery(id+"F6.opExtrude","SWEPT_FACE",FACE,{"disambiguationData":[OSD([subQ0])]})]}),makeQuery(id+"F6.opExtrude","CAP_FACE",FACE,{"disambiguationData":[OSD([sQuery(id+"F4.wireOp",EDGE,"E31"),subQ0])],"isStart":true})],"blendedInto":[makeQuery(id+"F6.opExtrude","CAP_FACE",FACE,{"disambiguationData":[OSD([sQuery(id+"F4.wireOp",EDGE,"E31"),subQ0])],"isStart":true})]});}
            var Q3;
            {var subQ0=sQuery(id+"F4.wireOp",EDGE,"E32");Q3=makeQuery(id+"F14.opFillet","BLEND_EDGE",EDGE,{"blendedFrom":[makeQuery(id+"F6.boolean.opBoolean","INTERSECT",EDGE,{"derivedFrom":[makeQuery(id+"F2.opExtrude","SWEPT_FACE",FACE,{"disambiguationData":[OSD([sQuery(id+"F0.wireOp",EDGE,"E19")])]}),makeQuery(id+"F6.opExtrude","SWEPT_FACE",FACE,{"disambiguationData":[OSD([subQ0])]})]}),makeQuery(id+"F6.opExtrude","CAP_FACE",FACE,{"disambiguationData":[OSD([sQuery(id+"F4.wireOp",EDGE,"E30"),subQ0])],"isStart":true})],"blendedInto":[makeQuery(id+"F6.opExtrude","CAP_FACE",FACE,{"disambiguationData":[OSD([sQuery(id+"F4.wireOp",EDGE,"E30"),subQ0])],"isStart":true})]});}
            fillet(context, id + "F15", {"entities" : qUnion([Q0, Q1, Q2, Q3]), "radius" : 1 * mm, "tangentPropagation" : true, "allowEdgeOverflow" : false});
        }
        {
            var Q0;
            Q0=makeQuery(id+"F6.opExtrude","CAP_EDGE",EDGE,{"disambiguationData":[OSD([sQuery(id+"F4.wireOp",EDGE,"E31")])],"isStart":false});
            var Q1;
            Q1=makeQuery(id+"F6.opExtrude","CAP_EDGE",EDGE,{"disambiguationData":[OSD([sQuery(id+"F4.wireOp",EDGE,"E30")])],"isStart":false});
            var Q2;
            {var subQ0=sQuery(id+"F0.wireOp",EDGE,"E0.rect.top");var subQ3=sQuery(id+"F0.wireOp",EDGE,"E0.rect.right");var subQ4=sQuery(id+"F0.wireOp",EDGE,"E6");var subQ5=makeQuery(id+"F2.opExtrude","SWEPT_FACE",FACE,{"disambiguationData":[OSD([subQ0]),TDD([makeQuery(id+"F0.imprint","IMPRINT",EDGE,{"disambiguationData":[TD([[makeQuery(id+"F0.imprint","INTERSECT",VERTEX,{"derivedFrom":[subQ0,subQ3,subQ4]}),1.0]])],"derivedFrom":subQ0})])]});var subQ6=sQuery(id+"F4.wireOp",EDGE,"E30");var subQ7=sQuery(id+"F4.wireOp",EDGE,"E32");Q2=makeQuery(id+"F5.boolean.opBoolean","INTERSECT",EDGE,{"derivedFrom":[makeQuery(id+"F7.boolean.opBoolean","MERGE",FACE,{"derivedFrom":[makeQuery(id+"F6.boolean.opBoolean","SPLIT",FACE,{"disambiguationData":[TD([makeQuery(id+"F6.opExtrude","SWEPT_FACE",FACE,{"disambiguationData":[OSD([subQ6])]})])],"derivedFrom":subQ5}),makeQuery(id+"F6.boolean.opBoolean","SPLIT",FACE,{"disambiguationData":[TD([makeQuery(id+"F2.opExtrude","SWEPT_FACE",FACE,{"disambiguationData":[OSD([sQuery(id+"F0.wireOp",EDGE,"E5.rect.right")])]})])],"derivedFrom":subQ5}),makeQuery(id+"F7.opExtrude","CAP_FACE",FACE,{"disambiguationData":[OSD([subQ6,subQ7])],"isStart":true})]}),makeQuery(id+"F5.opExtrude","SWEPT_FACE",FACE,{"disambiguationData":[OSD([subQ6])]})]});}
            var Q3;
            {var subQ0=sQuery(id+"F0.wireOp",EDGE,"E0.rect.top");var subQ3=sQuery(id+"F0.wireOp",EDGE,"E0.rect.left");var subQ4=sQuery(id+"F0.wireOp",EDGE,"E4");var subQ5=makeQuery(id+"F2.opExtrude","SWEPT_FACE",FACE,{"disambiguationData":[OSD([subQ0]),TDD([makeQuery(id+"F0.imprint","IMPRINT",EDGE,{"disambiguationData":[TD([[makeQuery(id+"F0.imprint","INTERSECT",VERTEX,{"derivedFrom":[subQ0,subQ3,subQ4]}),-1.0]])],"derivedFrom":subQ0})])]});var subQ6=sQuery(id+"F4.wireOp",EDGE,"E31");var subQ7=sQuery(id+"F4.wireOp",EDGE,"E33");var subQ8=sQuery(id+"F0.wireOp",EDGE,"E3");Q3=makeQuery(id+"F5.boolean.opBoolean","INTERSECT",EDGE,{"derivedFrom":[makeQuery(id+"F7.boolean.opBoolean","MERGE",FACE,{"derivedFrom":[makeQuery(id+"F6.boolean.opBoolean","SPLIT",FACE,{"disambiguationData":[TD([makeQuery(id+"F6.opExtrude","SWEPT_FACE",FACE,{"disambiguationData":[OSD([subQ6])]})])],"derivedFrom":subQ5}),makeQuery(id+"F6.boolean.opBoolean","SPLIT",FACE,{"disambiguationData":[TD([makeQuery(id+"F2.opExtrude","SWEPT_FACE",FACE,{"disambiguationData":[OSD([subQ8])]})])],"derivedFrom":subQ5}),makeQuery(id+"F7.opExtrude","CAP_FACE",FACE,{"disambiguationData":[OSD([subQ6,subQ7])],"isStart":true})]}),makeQuery(id+"F5.opExtrude","SWEPT_FACE",FACE,{"disambiguationData":[OSD([subQ6])]})]});}
            var Q4;
            {var subQ0=sQuery(id+"F0.wireOp",EDGE,"E0.rect.bottom");var subQ3=sQuery(id+"F0.wireOp",EDGE,"E0.rect.left");var subQ4=sQuery(id+"F0.wireOp",EDGE,"E3");var subQ5=makeQuery(id+"F2.opExtrude","SWEPT_FACE",FACE,{"disambiguationData":[OSD([subQ0]),TDD([makeQuery(id+"F0.imprint","IMPRINT",EDGE,{"disambiguationData":[TD([[makeQuery(id+"F0.imprint","INTERSECT",VERTEX,{"derivedFrom":[subQ0,subQ3,subQ4]}),-1.0]])],"derivedFrom":subQ0})])]});var subQ6=sQuery(id+"F4.wireOp",EDGE,"E31");var subQ7=sQuery(id+"F4.wireOp",EDGE,"E33");Q4=makeQuery(id+"F5.boolean.opBoolean","INTERSECT",EDGE,{"derivedFrom":[makeQuery(id+"F7.boolean.opBoolean","MERGE",FACE,{"derivedFrom":[makeQuery(id+"F6.boolean.opBoolean","SPLIT",FACE,{"disambiguationData":[TD([makeQuery(id+"F6.opExtrude","SWEPT_FACE",FACE,{"disambiguationData":[OSD([subQ6])]})])],"derivedFrom":subQ5}),makeQuery(id+"F6.boolean.opBoolean","SPLIT",FACE,{"disambiguationData":[TD([makeQuery(id+"F2.opExtrude","SWEPT_FACE",FACE,{"disambiguationData":[OSD([subQ4])]})])],"derivedFrom":subQ5}),makeQuery(id+"F7.opExtrude","CAP_FACE",FACE,{"disambiguationData":[OSD([subQ6,subQ7])],"isStart":false})]}),makeQuery(id+"F5.opExtrude","SWEPT_FACE",FACE,{"disambiguationData":[OSD([subQ6])]})]});}
            var Q5;
            {var subQ0=sQuery(id+"F0.wireOp",EDGE,"E0.rect.bottom");var subQ1=sQuery(id+"F0.wireOp",EDGE,"E5.rect.right");var subQ3=sQuery(id+"F0.wireOp",EDGE,"E0.rect.right");var subQ4=sQuery(id+"F0.wireOp",EDGE,"E7");var subQ5=makeQuery(id+"F2.opExtrude","SWEPT_FACE",FACE,{"disambiguationData":[OSD([subQ0]),TDD([makeQuery(id+"F0.imprint","IMPRINT",EDGE,{"disambiguationData":[TD([[makeQuery(id+"F0.imprint","INTERSECT",VERTEX,{"derivedFrom":[subQ0,subQ3,subQ4]}),1.0]])],"derivedFrom":subQ0})])]});var subQ6=sQuery(id+"F4.wireOp",EDGE,"E30");var subQ7=sQuery(id+"F4.wireOp",EDGE,"E32");Q5=makeQuery(id+"F5.boolean.opBoolean","INTERSECT",EDGE,{"derivedFrom":[makeQuery(id+"F7.boolean.opBoolean","MERGE",FACE,{"derivedFrom":[makeQuery(id+"F6.boolean.opBoolean","SPLIT",FACE,{"disambiguationData":[TD([makeQuery(id+"F6.opExtrude","SWEPT_FACE",FACE,{"disambiguationData":[OSD([subQ6])]})])],"derivedFrom":subQ5}),makeQuery(id+"F6.boolean.opBoolean","SPLIT",FACE,{"disambiguationData":[TD([makeQuery(id+"F2.opExtrude","SWEPT_FACE",FACE,{"disambiguationData":[OSD([subQ1])]})])],"derivedFrom":subQ5}),makeQuery(id+"F7.opExtrude","CAP_FACE",FACE,{"disambiguationData":[OSD([subQ6,subQ7])],"isStart":false})]}),makeQuery(id+"F5.opExtrude","SWEPT_FACE",FACE,{"disambiguationData":[OSD([subQ6])]})]});}
            fillet(context, id + "F16", {"entities" : qUnion([Q0, Q1, Q2, Q3, Q4, Q5]), "radius" : 0.5 * mm, "tangentPropagation" : true, "allowEdgeOverflow" : false});
        }
        {
            var Q0;
            Q0=makeQuery(id+"F8.boolean.opBoolean","COPY",FACE,{"disambiguationData":[OD(1.0)],"derivedFrom":makeQuery(id+"F8.opExtrude","SWEPT_FACE",FACE,{"disambiguationData":[OSD([sQuery(id+"F4.wireOp",EDGE,"E35")])]})});
            var Q1;
            Q1=makeQuery(id+"F8.boolean.opBoolean","COPY",FACE,{"disambiguationData":[OD(1.0)],"derivedFrom":makeQuery(id+"F8.opExtrude","SWEPT_FACE",FACE,{"disambiguationData":[OSD([sQuery(id+"F4.wireOp",EDGE,"E34")])]})});
            var Q2;
            Q2=makeQuery(id+"F8.boolean.opBoolean","COPY",FACE,{"disambiguationData":[OD(0.0)],"derivedFrom":makeQuery(id+"F8.opExtrude","SWEPT_FACE",FACE,{"disambiguationData":[OSD([sQuery(id+"F4.wireOp",EDGE,"E34")])]})});
            var Q3;
            Q3=makeQuery(id+"F8.boolean.opBoolean","COPY",FACE,{"disambiguationData":[OD(0.0)],"derivedFrom":makeQuery(id+"F8.opExtrude","SWEPT_FACE",FACE,{"disambiguationData":[OSD([sQuery(id+"F4.wireOp",EDGE,"E35")])]})});
            fillet(context, id + "F17", {"entities" : qUnion([Q0, Q1, Q2, Q3]), "radius" : 2 * mm, "tangentPropagation" : true, "allowEdgeOverflow" : false});
        }
    });
